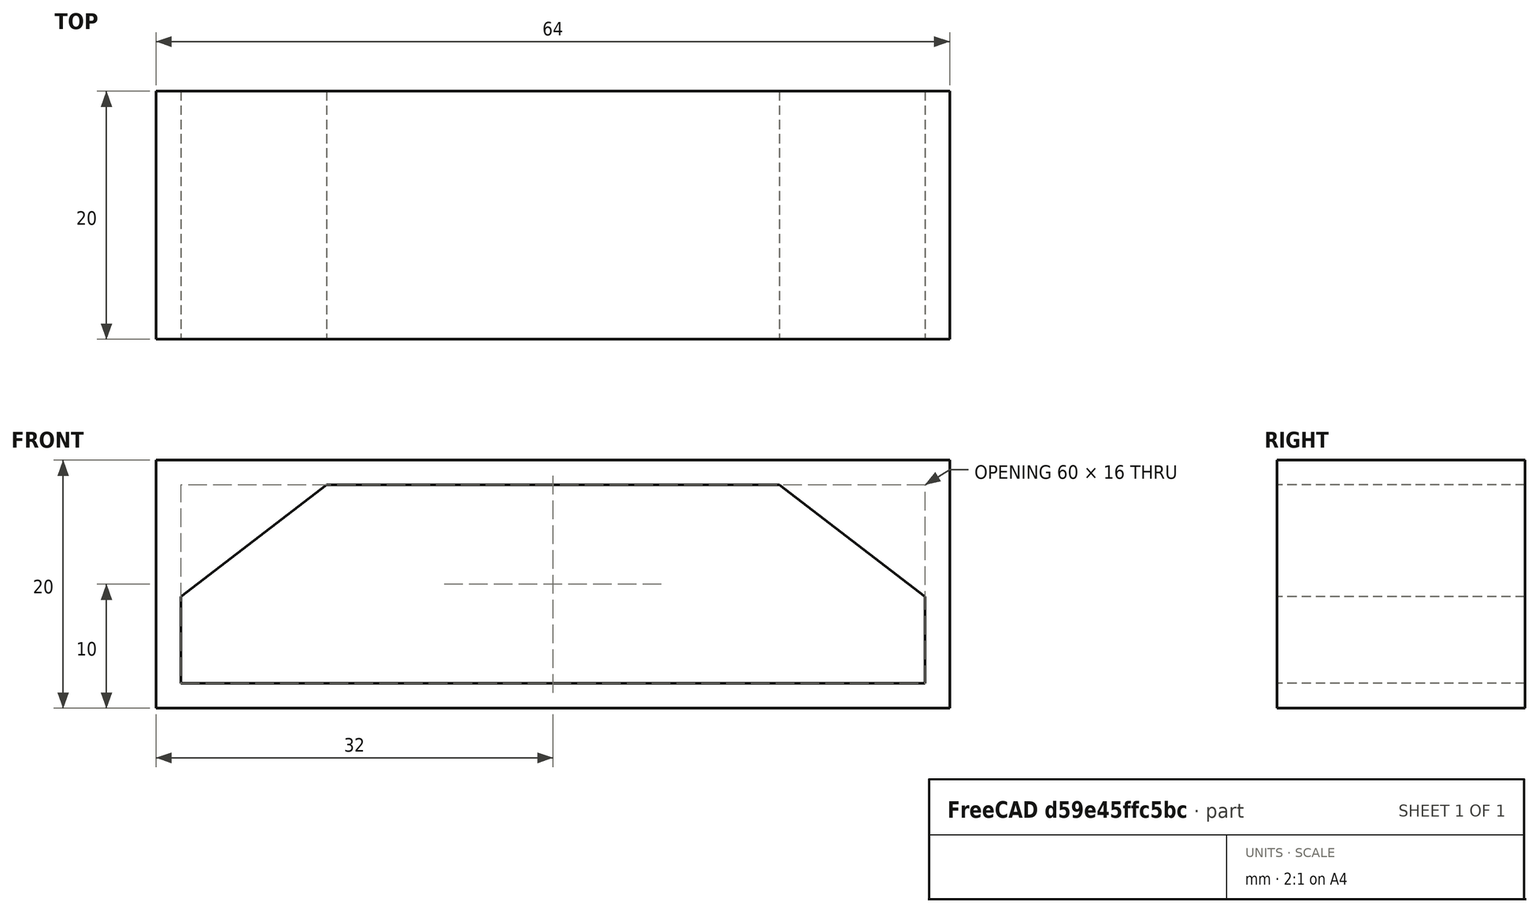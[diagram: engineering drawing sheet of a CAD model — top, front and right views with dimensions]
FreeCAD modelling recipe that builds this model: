
FCSTD DOCUMENT  (FreeCAD 0.21R33771 (Git))
Label: SpinningBikePhoneStand
License: All rights reserved
LicenseURL: http://en.wikipedia.org/wiki/All_rights_reserved
objects: Sketcher::SketchObject×2, PartDesign::Pad×1, PartDesign::Body×1
note: 5 computed .brp shape members not serialized (recipe doc carries the construction recipe); baked Part::Feature solids carry a one-line shape summary decoded from their .brp

FEATURE [Sketcher::SketchObject] Sketch
  FullyConstrained = true
  MapMode = 5
  Placement = pos=(0,0,0) rot=(1,0,0;1.5708rad)
  Support = -> [XZ_Plane]
  sketch-geometry (10):
    g0: LineSegment StartX=-18.25 StartY=16 StartZ=0 EndX=18.25 EndY=16 EndZ=0
    g1: LineSegment StartX=18.25 StartY=16 StartZ=0 EndX=30 EndY=7 EndZ=0
    g2: LineSegment StartX=30 StartY=7 StartZ=0 EndX=30 EndY=0 EndZ=0
    g3: LineSegment StartX=-18.25 StartY=16 StartZ=0 EndX=-30 EndY=7 EndZ=0
    g4: LineSegment StartX=-30 StartY=7 StartZ=0 EndX=-30 EndY=0 EndZ=0
    g5: LineSegment StartX=-30 StartY=0 StartZ=0 EndX=30 EndY=0 EndZ=0
    g6: LineSegment StartX=-32 StartY=-2 StartZ=0 EndX=32 EndY=-2 EndZ=0
    g7: LineSegment StartX=32 StartY=-2 StartZ=0 EndX=32 EndY=18 EndZ=0
    g8: LineSegment StartX=32 StartY=18 StartZ=0 EndX=-32 EndY=18 EndZ=0
    g9: LineSegment StartX=-32 StartY=18 StartZ=0 EndX=-32 EndY=-2 EndZ=0
  constraints (28):
    c: Coincident(g1,g0)
    c: Coincident(g2,g1)
    c: PointOnObject(g2,g-1)
    c: Vertical(g2)
    c: Coincident(g3,g0)
    c: Coincident(g4,g3)
    c: Coincident(g5,g4)
    c: Coincident(g5,g2)
    c: Vertical(g4)
    c: Symmetric(g0,g0,g-2)
    c: Horizontal(g3,g1)
    c: Symmetric(g4,g2,g-1)
    c: DistanceY(g2,g2) = 7
    c: DistanceX(g5,g5) = 60
    c: DistanceY(g-1,g0) = 16
    c: DistanceX(g0,g0) = 36.5
    c: Horizontal(g6)
    c: Coincident(g7,g6)
    c: Vertical(g7)
    c: Horizontal(g8)
    c: Coincident(g9,g6)
    c: Vertical(g9)
    c: DistanceY(g6,g2) = 2
    c: DistanceX(g2,g6) = 2
    c: DistanceX(g6,g4) = 2
    c: DistanceY(g0,g8) = 2
    c: Coincident(g8,g9)
    c: Coincident(g7,g8)
FEATURE [PartDesign::Pad] Pad
  Direction = (0,-1,2e-16)
  Length = 20
  Length2 = 10
  Placement = pos=(0,0,0) rot=(1,0,0;1.5708rad)
  Profile = -> Sketch
  ReferenceAxis = -> Sketch [N_Axis]
  Type = 0
FEATURE [Sketcher::SketchObject] Sketch001
  ExternalGeometry = -> [Pad]
  FullyConstrained = true
  MapMode = 5
  Placement = pos=(-32,0,0) rot=(0.707107,0,-0.707107;3.14159rad)
  Support = -> [Pad]
  sketch-geometry (8):
    g0: LineSegment StartX=-18 StartY=20 StartZ=0 EndX=-10.9289 EndY=27.0711 EndZ=0
    g1: LineSegment StartX=-10.9289 StartY=27.0711 StartZ=0 EndX=-9.51472 EndY=25.6569 EndZ=0
    g2: LineSegment StartX=-9.51472 StartY=25.6569 StartZ=0 EndX=-13.1716 EndY=22 EndZ=0
    g3: LineSegment StartX=-13.1716 StartY=22 StartZ=0 EndX=1.17157 EndY=22 EndZ=0
    g4: LineSegment StartX=2 StartY=20 StartZ=0 EndX=45.0122 EndY=63.0122 EndZ=0
    g5: LineSegment StartX=45.0122 StartY=63.0122 StartZ=0 EndX=43.598 EndY=64.4264 EndZ=0
    g6: LineSegment StartX=43.598 StartY=64.4264 StartZ=0 EndX=1.17157 EndY=22 EndZ=0
    g7: LineSegment StartX=-18 StartY=20 StartZ=0 EndX=2 EndY=20 EndZ=0
  constraints (22):
    c: Coincident(g0,g-3)
    c: Coincident(g1,g0)
    c: Coincident(g2,g1)
    c: Coincident(g3,g2)
    c: Horizontal(g3)
    c: Coincident(g4,g-5)
    c: Coincident(g5,g4)
    c: Coincident(g6,g5)
    c: Coincident(g6,g3)
    c: Coincident(g7,g0)
    c: Coincident(g7,g4)
    c: Angle(g7,g0) = 0.785398
    c: Parallel(g0,g2)
    c: Parallel(g2,g6)
    c: Parallel(g6,g4)
    c: Angle(g0,g1) = 1.5708
    c: Parallel(g5,g1)
    c: DistanceY(g4,g3) = 2
    c: Distance(g1,g0) = 2
    c: Distance(g4,g5) = 2
    c: Distance(g6) = 60
    c: Distance(g0,g0) = 10
FEATURE [PartDesign::Body] Body
  Group = -> [Sketch,Pad,Sketch001]
  Origin = -> Origin
  Tip = -> Pad
